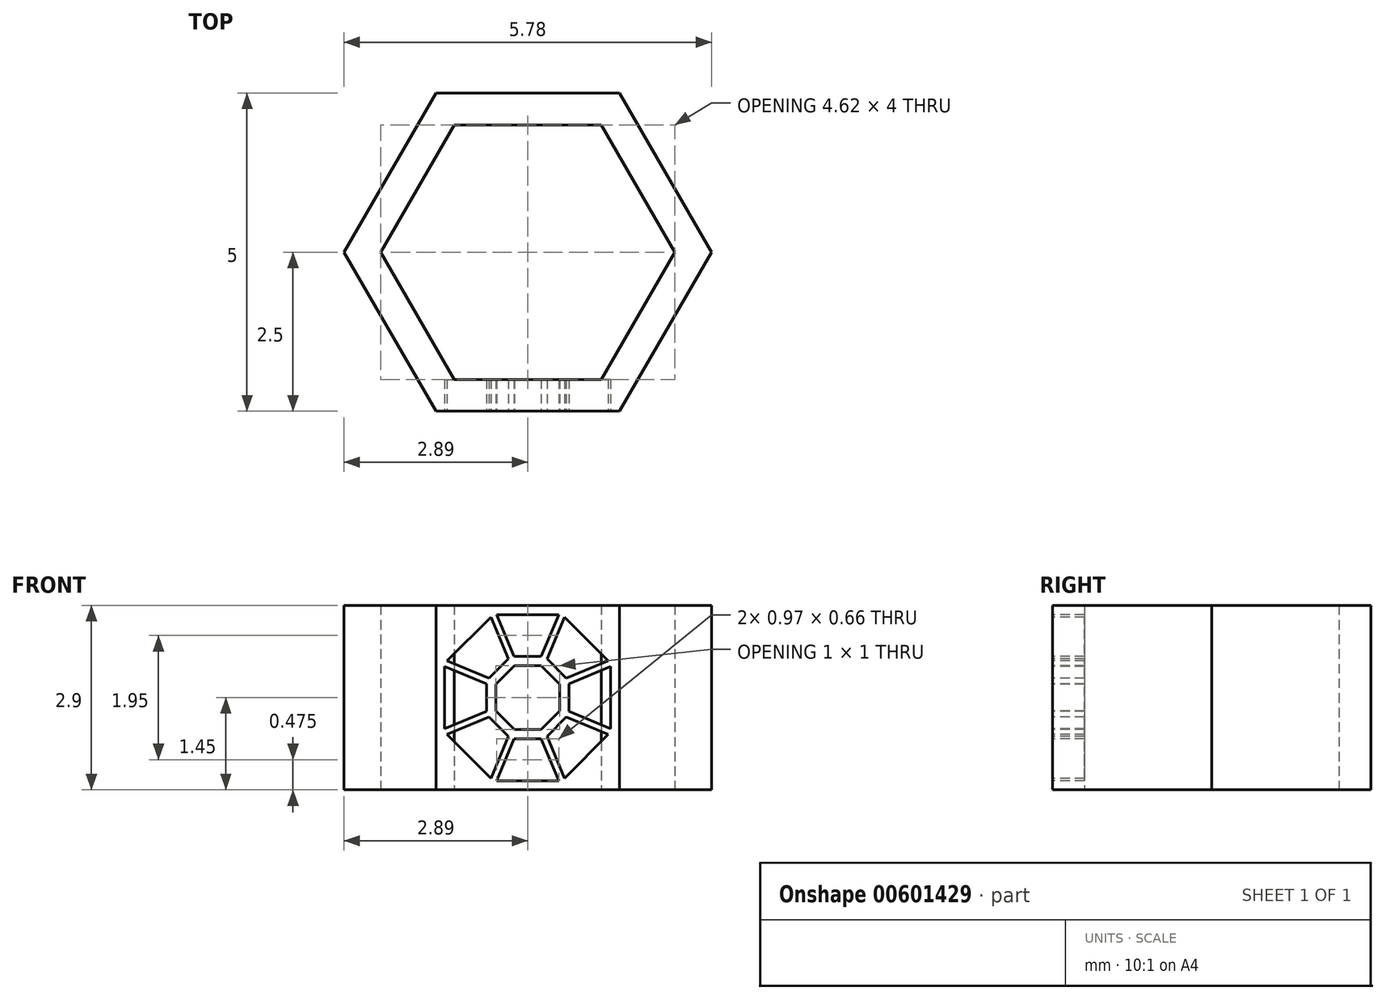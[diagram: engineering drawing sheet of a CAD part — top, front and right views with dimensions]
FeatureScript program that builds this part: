
annotation { "Feature Type Name" : "Feature", "Feature Type Description" : "" }
export const myFeature = defineFeature(function(context is Context, id is Id, definition is map)
    precondition{}
    {
        {
            assignVariable(context, id + "F0", {"name" : "B", "anyValue" : 2.9});
        }
        {
            var Q0;
            Q0=qCreatedBy(makeId("Top.planeOp"),FACE);
            var sketch = newSketch(context, id + "F1", { "sketchPlane" : qUnion([Q0])});
            skCircle(sketch, "E0.cCircle", {"center": v(0, 0) * mm, "radius": 2.5 * mm, "construction": true});
            skLineSegment(sketch, "E0.0", {"start": v(1.44, -2.5) * mm, "end": v(-1.44, -2.5) * mm});
            skLineSegment(sketch, "E0.1", {"start": v(-1.44, -2.5) * mm, "end": v(-2.89, 0) * mm});
            skLineSegment(sketch, "E0.2", {"start": v(-2.89, 0) * mm, "end": v(-1.44, 2.5) * mm});
            skLineSegment(sketch, "E0.3", {"start": v(-1.44, 2.5) * mm, "end": v(1.44, 2.5) * mm});
            skLineSegment(sketch, "E0.4", {"start": v(1.44, 2.5) * mm, "end": v(2.89, 0) * mm});
            skLineSegment(sketch, "E0.5", {"start": v(2.89, 0) * mm, "end": v(1.44, -2.5) * mm});
            skPoint(sketch, "E0.0.midPoint", {"position": v(0, -2.5) * mm});
            skLineSegment(sketch, "E1.0", {"start": v(-1.15, -2) * mm, "end": v(-2.3, 0) * mm});
            skLineSegment(sketch, "E1.1", {"start": v(-1.15, 2) * mm, "end": v(1.15, 2) * mm});
            skLineSegment(sketch, "E1.2", {"start": v(1.15, 2) * mm, "end": v(2.3, 0) * mm});
            skLineSegment(sketch, "E1.3", {"start": v(-2.3, 0) * mm, "end": v(-1.15, 2) * mm});
            skLineSegment(sketch, "E1.4", {"start": v(2.3, 0) * mm, "end": v(1.15, -2) * mm});
            skLineSegment(sketch, "E1.5", {"start": v(1.15, -2) * mm, "end": v(-1.15, -2) * mm});
            skSolve(sketch);
        }
        {
            var Q0;
            Q0 = qSketchRegion(id + "F1", true);
            extrude(context, id + "F2", {"entities" : qUnion([Q0]), "depth" : (getVariable(context, 'B')) * mm, "offsetDistance" : 25 * mm});
        }
        {
            var Q0;
            Q0=makeQuery(id+"F2.opExtrude","SWEPT_FACE",FACE,{"disambiguationData":[OSD([sQuery(id+"F1.wireOp",EDGE,"E0.0")])]});
            var sketch = newSketch(context, id + "F3", { "sketchPlane" : qUnion([Q0])});
            skLineSegment(sketch, "E2", {"start": v(-1.44, 1.45) * mm, "end": v(1.44, 1.45) * mm, "construction": true});
            skCircle(sketch, "E3.cCircle", {"center": v(0, 1.45) * mm, "radius": 1.45 * mm, "construction": true});
            skPoint(sketch, "E3.cCircle.perimeterSnap0", {"position": v(0, 1.45) * mm});
            skLineSegment(sketch, "E3.0", {"start": v(-0.6, 2.9) * mm, "end": v(0.6, 2.9) * mm});
            skLineSegment(sketch, "E3.1", {"start": v(0.6, 2.9) * mm, "end": v(1.45, 2.05) * mm});
            skLineSegment(sketch, "E3.2", {"start": v(1.45, 2.05) * mm, "end": v(1.45, 0.85) * mm});
            skLineSegment(sketch, "E3.3", {"start": v(1.45, 0.85) * mm, "end": v(0.6, 0) * mm});
            skLineSegment(sketch, "E3.4", {"start": v(0.6, 0) * mm, "end": v(-0.6, 0) * mm});
            skLineSegment(sketch, "E3.5", {"start": v(-0.6, 0) * mm, "end": v(-1.45, 0.85) * mm});
            skLineSegment(sketch, "E3.6", {"start": v(-1.45, 0.85) * mm, "end": v(-1.45, 2.05) * mm});
            skLineSegment(sketch, "E3.7", {"start": v(-1.45, 2.05) * mm, "end": v(-0.6, 2.9) * mm});
            skPoint(sketch, "E3.0.midPoint", {"position": v(0, 2.9) * mm});
            skPoint(sketch, "E3.0.midPoint.positionSnap0", {"position": v(0, 1.45) * mm});
            skLineSegment(sketch, "E4.0", {"start": v(-1.3, 0.9) * mm, "end": v(-1.3, 2) * mm});
            skLineSegment(sketch, "E4.1", {"start": v(-0.54, 0.15) * mm, "end": v(-1.3, 0.9) * mm});
            skLineSegment(sketch, "E4.2", {"start": v(-1.3, 2) * mm, "end": v(-0.54, 2.75) * mm});
            skLineSegment(sketch, "E4.3", {"start": v(0.54, 0.15) * mm, "end": v(-0.54, 0.15) * mm});
            skLineSegment(sketch, "E4.4", {"start": v(-0.54, 2.75) * mm, "end": v(0.54, 2.75) * mm});
            skLineSegment(sketch, "E4.5", {"start": v(0.54, 2.75) * mm, "end": v(1.3, 2) * mm});
            skLineSegment(sketch, "E4.6", {"start": v(1.3, 2) * mm, "end": v(1.3, 0.9) * mm});
            skLineSegment(sketch, "E4.7", {"start": v(1.3, 0.9) * mm, "end": v(0.54, 0.15) * mm});
            skCircle(sketch, "E5.cCircle", {"center": v(0, 1.45) * mm, "radius": 0.65 * mm, "construction": true});
            skLineSegment(sketch, "E5.0", {"start": v(-0.27, 2.1) * mm, "end": v(0.27, 2.1) * mm});
            skLineSegment(sketch, "E5.1", {"start": v(0.27, 2.1) * mm, "end": v(0.65, 1.72) * mm});
            skLineSegment(sketch, "E5.2", {"start": v(0.65, 1.72) * mm, "end": v(0.65, 1.18) * mm});
            skLineSegment(sketch, "E5.3", {"start": v(0.65, 1.18) * mm, "end": v(0.27, 0.8) * mm});
            skLineSegment(sketch, "E5.4", {"start": v(0.27, 0.8) * mm, "end": v(-0.27, 0.8) * mm});
            skLineSegment(sketch, "E5.5", {"start": v(-0.27, 0.8) * mm, "end": v(-0.64, 1.18) * mm});
            skLineSegment(sketch, "E5.6", {"start": v(-0.64, 1.18) * mm, "end": v(-0.64, 1.72) * mm});
            skLineSegment(sketch, "E5.7", {"start": v(-0.64, 1.72) * mm, "end": v(-0.27, 2.1) * mm});
            skPoint(sketch, "E5.0.midPoint", {"position": v(0, 2.1) * mm});
            skCircle(sketch, "E6.cCircle", {"center": v(0, 1.45) * mm, "radius": 0.5 * mm, "construction": true});
            skLineSegment(sketch, "E6.0", {"start": v(-0.2, 1.95) * mm, "end": v(0.2, 1.95) * mm});
            skLineSegment(sketch, "E6.1", {"start": v(0.2, 1.95) * mm, "end": v(0.5, 1.66) * mm});
            skLineSegment(sketch, "E6.2", {"start": v(0.5, 1.66) * mm, "end": v(0.5, 1.24) * mm});
            skLineSegment(sketch, "E6.3", {"start": v(0.5, 1.24) * mm, "end": v(0.2, 0.95) * mm});
            skLineSegment(sketch, "E6.4", {"start": v(0.2, 0.95) * mm, "end": v(-0.2, 0.95) * mm});
            skLineSegment(sketch, "E6.5", {"start": v(-0.2, 0.95) * mm, "end": v(-0.5, 1.24) * mm});
            skLineSegment(sketch, "E6.6", {"start": v(-0.5, 1.24) * mm, "end": v(-0.5, 1.66) * mm});
            skLineSegment(sketch, "E6.7", {"start": v(-0.5, 1.66) * mm, "end": v(-0.2, 1.95) * mm});
            skPoint(sketch, "E6.0.midPoint", {"position": v(0, 1.95) * mm});
            skLineSegment(sketch, "E7", {"start": v(-0.54, 2.75) * mm, "end": v(-0.27, 2.1) * mm, "construction": true});
            skLineSegment(sketch, "E8", {"start": v(0.27, 2.1) * mm, "end": v(0.54, 2.75) * mm, "construction": true});
            skLineSegment(sketch, "E9", {"start": v(0.65, 1.72) * mm, "end": v(1.3, 2) * mm, "construction": true});
            skLineSegment(sketch, "E10", {"start": v(0.65, 1.18) * mm, "end": v(1.3, 0.9) * mm, "construction": true});
            skLineSegment(sketch, "E11", {"start": v(0.27, 0.8) * mm, "end": v(0.54, 0.15) * mm, "construction": true});
            skLineSegment(sketch, "E12", {"start": v(-0.27, 0.8) * mm, "end": v(-0.54, 0.15) * mm, "construction": true});
            skLineSegment(sketch, "E13", {"start": v(-0.64, 1.18) * mm, "end": v(-1.3, 0.9) * mm, "construction": true});
            skLineSegment(sketch, "E14", {"start": v(-0.64, 1.72) * mm, "end": v(-1.3, 2) * mm, "construction": true});
            skLineSegment(sketch, "E15", {"start": v(-0.6, 1.76) * mm, "end": v(-1.27, 2.03) * mm});
            skLineSegment(sketch, "E16", {"start": v(-0.21, 2.1) * mm, "end": v(-0.49, 2.75) * mm});
            skLineSegment(sketch, "E17", {"start": v(0.3, 2.06) * mm, "end": v(0.58, 2.72) * mm});
            skLineSegment(sketch, "E18", {"start": v(0.21, 2.1) * mm, "end": v(0.49, 2.75) * mm});
            skLineSegment(sketch, "E19", {"start": v(-0.3, 2.06) * mm, "end": v(-0.58, 2.72) * mm});
            skLineSegment(sketch, "E20", {"start": v(-0.4, 2.42) * mm, "end": v(-0.36, 2.44) * mm, "construction": true});
            skLineSegment(sketch, "E21", {"start": v(-0.4, 2.43) * mm, "end": v(-0.45, 2.4) * mm, "construction": true});
            skLineSegment(sketch, "E22", {"start": v(0.4, 2.42) * mm, "end": v(0.36, 2.44) * mm, "construction": true});
            skLineSegment(sketch, "E23", {"start": v(0.4, 2.42) * mm, "end": v(0.45, 2.4) * mm, "construction": true});
            skLineSegment(sketch, "E24", {"start": v(-0.64, 1.66) * mm, "end": v(-1.3, 1.94) * mm});
            skLineSegment(sketch, "E25", {"start": v(-0.64, 1.24) * mm, "end": v(-1.3, 0.96) * mm});
            skLineSegment(sketch, "E26", {"start": v(-0.6, 1.14) * mm, "end": v(-1.27, 0.87) * mm});
            skLineSegment(sketch, "E27", {"start": v(-0.3, 0.84) * mm, "end": v(-0.58, 0.18) * mm});
            skLineSegment(sketch, "E28", {"start": v(-0.21, 0.8) * mm, "end": v(-0.49, 0.15) * mm});
            skLineSegment(sketch, "E29", {"start": v(0.21, 0.8) * mm, "end": v(0.49, 0.15) * mm});
            skLineSegment(sketch, "E30", {"start": v(0.58, 0.18) * mm, "end": v(0.3, 0.84) * mm});
            skLineSegment(sketch, "E31", {"start": v(0.6, 1.14) * mm, "end": v(1.27, 0.87) * mm});
            skLineSegment(sketch, "E32", {"start": v(0.64, 1.24) * mm, "end": v(1.3, 0.96) * mm});
            skLineSegment(sketch, "E33", {"start": v(0.64, 1.66) * mm, "end": v(1.3, 1.94) * mm});
            skLineSegment(sketch, "E34", {"start": v(1.27, 2.03) * mm, "end": v(0.6, 1.76) * mm});
            skLineSegment(sketch, "E35", {"start": v(0.97, 1.85) * mm, "end": v(0.96, 1.9) * mm, "construction": true});
            skLineSegment(sketch, "E36", {"start": v(0.97, 1.85) * mm, "end": v(1, 1.8) * mm, "construction": true});
            skLineSegment(sketch, "E37", {"start": v(0.98, 1.05) * mm, "end": v(1, 1.1) * mm, "construction": true});
            skLineSegment(sketch, "E38", {"start": v(0.4, 0.48) * mm, "end": v(0.45, 0.5) * mm, "construction": true});
            skLineSegment(sketch, "E39", {"start": v(0.4, 0.48) * mm, "end": v(0.36, 0.46) * mm, "construction": true});
            skLineSegment(sketch, "E40", {"start": v(-0.4, 0.48) * mm, "end": v(-0.36, 0.46) * mm, "construction": true});
            skPoint(sketch, "E41.endSnap0", {"position": v(-0.44, 0.51) * mm});
            skLineSegment(sketch, "E42", {"start": v(-0.4, 0.48) * mm, "end": v(-0.45, 0.5) * mm, "construction": true});
            skLineSegment(sketch, "E43", {"start": v(-0.97, 1.05) * mm, "end": v(-0.96, 1) * mm, "construction": true});
            skLineSegment(sketch, "E44", {"start": v(-0.97, 1.05) * mm, "end": v(-1, 1.1) * mm, "construction": true});
            skLineSegment(sketch, "E45", {"start": v(0.98, 1.05) * mm, "end": v(0.96, 1) * mm, "construction": true});
            skLineSegment(sketch, "E46", {"start": v(-0.97, 1.85) * mm, "end": v(-0.96, 1.9) * mm, "construction": true});
            skLineSegment(sketch, "E47", {"start": v(-0.97, 1.85) * mm, "end": v(-1, 1.8) * mm, "construction": true});
            skSolve(sketch);
        }
        {
            var Q0;
            {var subQ0=sQuery(id+"F3.wireOp",EDGE,"E16");Q0=makeQuery(id+"F3.imprint","IMPRINT",FACE,{"disambiguationData":[TD([[makeQuery(id+"F3.imprint","IMPRINT",EDGE,{"derivedFrom":subQ0}),-1.0]])]});}
            var Q1;
            {var subQ0=sQuery(id+"F3.wireOp",EDGE,"E17");Q1=makeQuery(id+"F3.imprint","IMPRINT",FACE,{"disambiguationData":[TD([[makeQuery(id+"F3.imprint","IMPRINT",EDGE,{"derivedFrom":subQ0}),-1.0]])]});}
            var Q2;
            {var subQ0=sQuery(id+"F3.wireOp",EDGE,"E32");Q2=makeQuery(id+"F3.imprint","IMPRINT",FACE,{"disambiguationData":[TD([[makeQuery(id+"F3.imprint","IMPRINT",EDGE,{"derivedFrom":subQ0}),1.0]])]});}
            var Q3;
            {var subQ0=sQuery(id+"F3.wireOp",EDGE,"E30");Q3=makeQuery(id+"F3.imprint","IMPRINT",FACE,{"disambiguationData":[TD([[makeQuery(id+"F3.imprint","IMPRINT",EDGE,{"derivedFrom":subQ0}),-1.0]])]});}
            var Q4;
            Q4=makeQuery(id+"F3.imprint","IMPRINT",FACE,{"disambiguationData":[TD([[makeQuery(id+"F3.imprint","IMPRINT",EDGE,{"derivedFrom":sQuery(id+"F3.wireOp",EDGE,"E6.0")}),-1.0]])]});
            var Q5;
            {var subQ0=sQuery(id+"F3.wireOp",EDGE,"E28");Q5=makeQuery(id+"F3.imprint","IMPRINT",FACE,{"disambiguationData":[TD([[makeQuery(id+"F3.imprint","IMPRINT",EDGE,{"derivedFrom":subQ0}),1.0]])]});}
            var Q6;
            {var subQ0=sQuery(id+"F3.wireOp",EDGE,"E26");Q6=makeQuery(id+"F3.imprint","IMPRINT",FACE,{"disambiguationData":[TD([[makeQuery(id+"F3.imprint","IMPRINT",EDGE,{"derivedFrom":subQ0}),1.0]])]});}
            var Q7;
            {var subQ0=sQuery(id+"F3.wireOp",EDGE,"E24");Q7=makeQuery(id+"F3.imprint","IMPRINT",FACE,{"disambiguationData":[TD([[makeQuery(id+"F3.imprint","IMPRINT",EDGE,{"derivedFrom":subQ0}),1.0]])]});}
            var Q8;
            {var subQ0=sQuery(id+"F3.wireOp",EDGE,"E15");Q8=makeQuery(id+"F3.imprint","IMPRINT",FACE,{"disambiguationData":[TD([[makeQuery(id+"F3.imprint","IMPRINT",EDGE,{"derivedFrom":subQ0}),-1.0]])]});}
            var Q9;
            Q9=makeQuery(id+"F2.opExtrude","SWEPT_FACE",FACE,{"disambiguationData":[OSD([sQuery(id+"F1.wireOp",EDGE,"E1.5")])]});
            extrude(context, id + "F4", {"entities" : qUnion([Q0, Q1, Q2, Q3, Q4, Q5, Q6, Q7, Q8]), "operationType" : NewBodyOperationType.REMOVE, "endBound" : BoundingType.UP_TO_SURFACE, "oppositeDirection" : true, "depth" : 25 * mm, "endBoundEntityFace" : qUnion([Q9]), "offsetDistance" : 25 * mm});
        }
        {
            var Q0;
            Q0=qCreatedBy(makeId("Front.planeOp"),FACE);
            var sketch = newSketch(context, id + "F5", { "sketchPlane" : qUnion([Q0])});
            skLineSegment(sketch, "E48", {"start": v(0, 0) * mm, "end": v(0, 6.4) * mm});
            skSolve(sketch);
        }
    });
